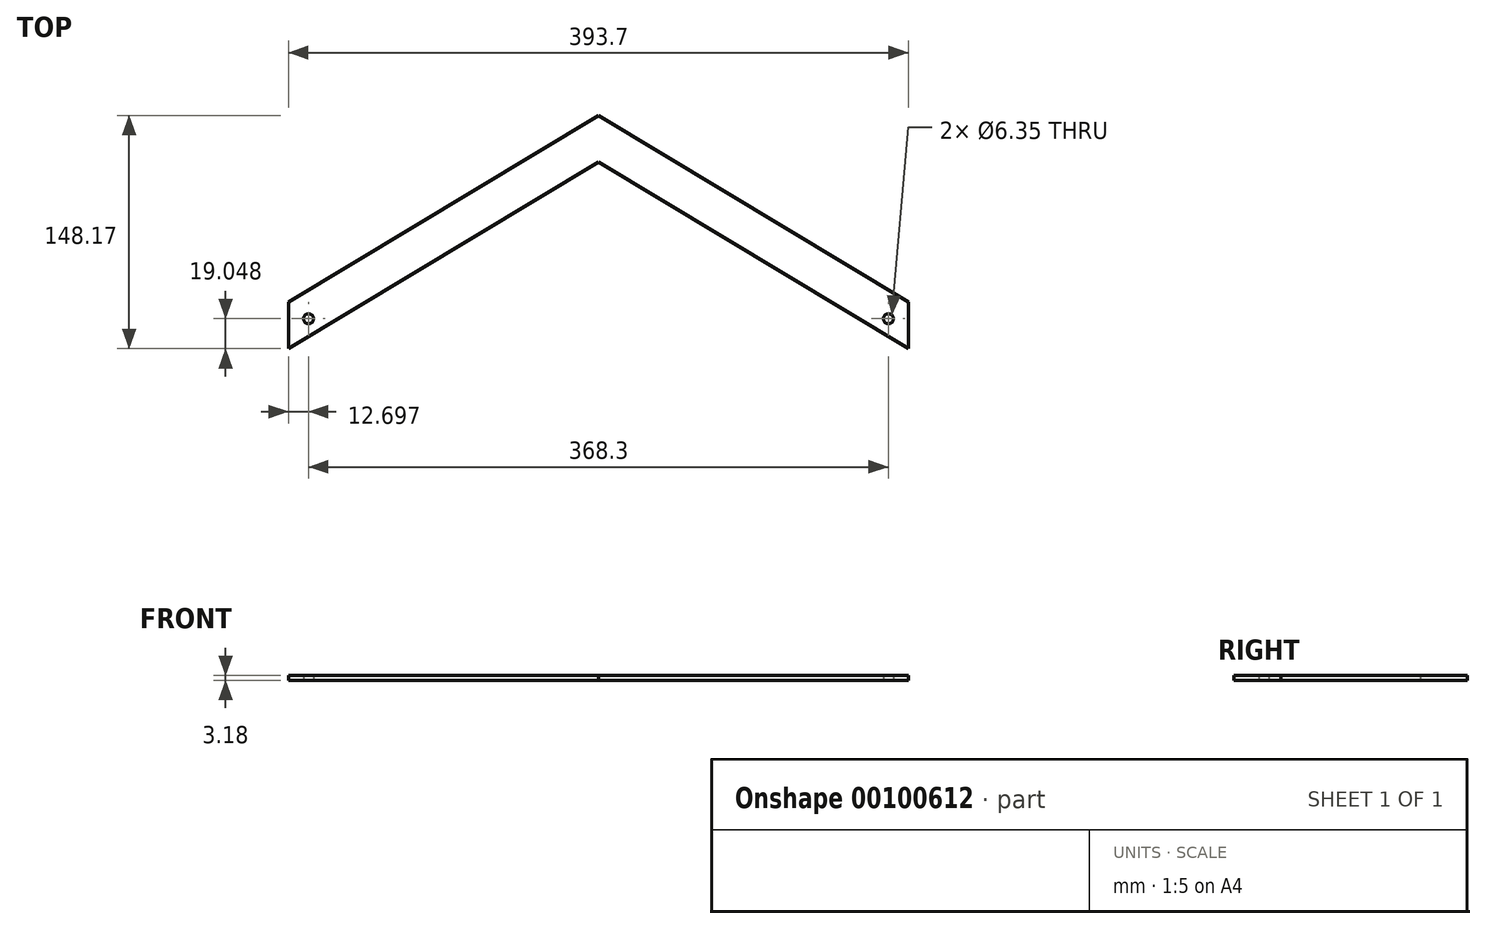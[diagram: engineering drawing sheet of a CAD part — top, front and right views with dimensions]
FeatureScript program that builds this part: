
annotation { "Feature Type Name" : "Feature", "Feature Type Description" : "" }
export const myFeature = defineFeature(function(context is Context, id is Id, definition is map)
    precondition{}
    {
        {
            var Q0;
            Q0=qCreatedBy(makeId("Top.planeOp"),FACE);
            var sketch = newSketch(context, id + "F0", { "sketchPlane" : qUnion([Q0])});
            skLineSegment(sketch, "E0", {"start": v(-80.9, 926.92) * mm, "end": v(-80.9, 1193.62) * mm});
            skLineSegment(sketch, "E1", {"start": v(-80.9, 1193.62) * mm, "end": v(312.8, 1193.62) * mm});
            skLineSegment(sketch, "E2", {"start": v(312.8, 1193.62) * mm, "end": v(312.8, 926.92) * mm});
            skLineSegment(sketch, "E3", {"start": v(312.8, 926.92) * mm, "end": v(-70.4, 926.92) * mm});
            skLineSegment(sketch, "E4", {"start": v(-80.9, 926.92) * mm, "end": v(-30.1, 926.92) * mm});
            skLineSegment(sketch, "E5", {"start": v(312.8, 1163.97) * mm, "end": v(312.8, 1193.62) * mm});
            skLineSegment(sketch, "E6", {"start": v(312.8, 926.92) * mm, "end": v(262, 926.92) * mm});
            skLineSegment(sketch, "E7", {"start": v(-80.9, 1163.97) * mm, "end": v(-80.9, 1193.62) * mm});
            skLineSegment(sketch, "E8", {"start": v(-80.9, 926.92) * mm, "end": v(312.8, 1163.97) * mm});
            skLineSegment(sketch, "E9", {"start": v(312.8, 1193.62) * mm, "end": v(-80.9, 956.57) * mm});
            skLineSegment(sketch, "E10", {"start": v(-80.9, 1193.62) * mm, "end": v(312.8, 956.57) * mm});
            skLineSegment(sketch, "E11", {"start": v(-80.9, 1163.97) * mm, "end": v(312.8, 926.92) * mm});
            skCircle(sketch, "E12", {"center": v(-68.2, 1174.57) * mm, "radius": 3.18 * mm});
            skCircle(sketch, "E13", {"center": v(-68.2, 945.97) * mm, "radius": 3.18 * mm});
            skLineSegment(sketch, "E14", {"start": v(115.95, 1193.62) * mm, "end": v(115.95, 926.92) * mm, "construction": true});
            skCircle(sketch, "E15.MirrorC", {"center": v(300.1, 1174.57) * mm, "radius": 3.18 * mm});
            skCircle(sketch, "E16.MirrorC", {"center": v(300.1, 945.97) * mm, "radius": 3.18 * mm});
            skSolve(sketch);
        }
        {
            var Q0;
            {var subQ0=sQuery(id+"F0.wireOp",EDGE,"E11");var subQ5=sQuery(id+"F0.wireOp",EDGE,"E8");var subQ6=makeQuery(id+"F0.imprint","INTERSECT",VERTEX,{"derivedFrom":[subQ5,subQ0]});Q0=makeQuery(id+"F0.imprint","IMPRINT",FACE,{"disambiguationData":[TD([[makeQuery(id+"F0.imprint","IMPRINT",EDGE,{"disambiguationData":[TD([[subQ6,-1.0]])],"derivedFrom":subQ5}),-1.0]])]});}
            var Q1;
            {var subQ0=sQuery(id+"F0.wireOp",EDGE,"E5");Q1=makeQuery(id+"F0.imprint","IMPRINT",FACE,{"disambiguationData":[TD([[makeQuery(id+"F0.imprint","IMPRINT",EDGE,{"derivedFrom":subQ0}),1.0]])]});}
            var Q2;
            {var subQ1=sQuery(id+"F0.wireOp",EDGE,"E0");var subQ3=sQuery(id+"F0.wireOp",EDGE,"E9");var subQ4=makeQuery(id+"F0.imprint","INTERSECT",VERTEX,{"derivedFrom":[subQ1,subQ3]});Q2=makeQuery(id+"F0.imprint","IMPRINT",FACE,{"disambiguationData":[TD([[makeQuery(id+"F0.imprint","IMPRINT",EDGE,{"disambiguationData":[TD([[subQ4,1.0]])],"derivedFrom":subQ3}),1.0]])]});}
            var Q3;
            {var subQ0=sQuery(id+"F0.wireOp",EDGE,"E7");Q3=makeQuery(id+"F0.imprint","IMPRINT",FACE,{"disambiguationData":[TD([[makeQuery(id+"F0.imprint","IMPRINT",EDGE,{"derivedFrom":subQ0}),-1.0]])]});}
            var Q4;
            {var subQ0=sQuery(id+"F0.wireOp",EDGE,"E11");var subQ1=sQuery(id+"F0.wireOp",EDGE,"E8");var subQ2=makeQuery(id+"F0.imprint","INTERSECT",VERTEX,{"derivedFrom":[subQ1,subQ0]});Q4=makeQuery(id+"F0.imprint","IMPRINT",FACE,{"disambiguationData":[TD([[makeQuery(id+"F0.imprint","IMPRINT",EDGE,{"disambiguationData":[TD([[subQ2,-1.0]])],"derivedFrom":subQ1}),1.0]])]});}
            extrude(context, id + "F1", {"entities" : qUnion([Q0, Q1, Q2, Q3, Q4]), "depth" : 3.17 * mm});
        }
    });
